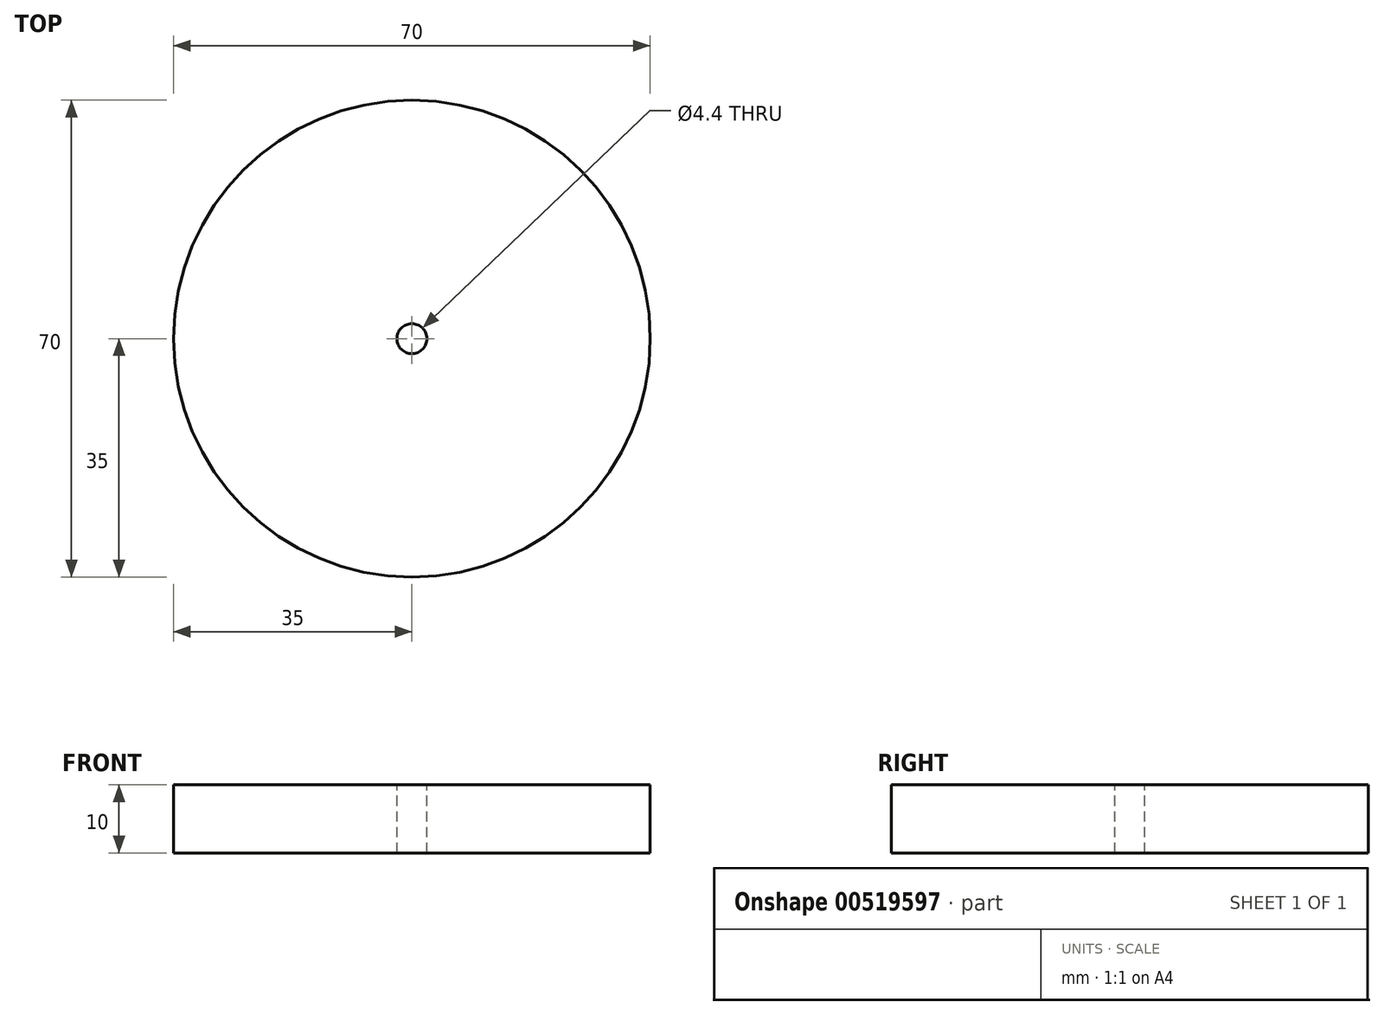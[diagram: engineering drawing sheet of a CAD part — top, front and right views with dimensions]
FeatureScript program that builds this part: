
annotation { "Feature Type Name" : "Feature", "Feature Type Description" : "" }
export const myFeature = defineFeature(function(context is Context, id is Id, definition is map)
    precondition{}
    {
        {
            var Q0;
            Q0=qCreatedBy(makeId("Top.planeOp"),FACE);
            var sketch = newSketch(context, id + "F0", { "sketchPlane" : qUnion([Q0])});
            skCircle(sketch, "E0", {"center": v(0, 0) * mm, "radius": 35 * mm});
            skSolve(sketch);
        }
        {
            var Q0;
            Q0=makeQuery(id+"F0.imprint","IMPRINT",FACE,{"disambiguationData":[TD([[makeQuery(id+"F0.imprint","IMPRINT",EDGE,{"derivedFrom":sQuery(id+"F0.wireOp",EDGE,"E0")}),1.0]])]});
            extrude(context, id + "F1", {"entities" : qUnion([Q0]), "depth" : 10 * mm, "offsetDistance" : 25.4 * mm});
        }
        {
            var Q0;
            Q0=makeQuery(id+"F1.opExtrude","CAP_FACE",FACE,{"disambiguationData":[OSD([sQuery(id+"F0.wireOp",EDGE,"E0")])],"isStart":false});
            var sketch = newSketch(context, id + "F2", { "sketchPlane" : qUnion([Q0])});
            skPoint(sketch, "E1", {"position": v(0, 0) * mm});
            skSolve(sketch);
        }
        {
            var Q0;
            Q0=sQuery(id+"F2.wireOp",VERTEX,"E1");
            var Q1;
            Q1=makeQuery(id+"F1.opExtrude","SWEPT_BODY",BODY,{"disambiguationData":[OSD([sQuery(id+"F0.wireOp",EDGE,"E0")])]});
            hole(context, id + "F3", {"style" : HoleStyle.SIMPLE, "endStyle" : HoleEndStyle.THROUGH, "standardTappedOrClearance" : lookupTablePath({ "fit" : "Normal", "standard" : "ISO", "engagement" : "75%", "pitch" : "0.8 mm", "size" : "M4", "type" : "Clearance" }), "standardBlindInLast" : lookupTablePath({ "fit" : "Standard", "standard" : "ISO", "engagement" : "75%", "pitch" : "0.8 mm", "size" : "M4", "type" : "Clearance" }), "holeDiameter" : 4.4 * mm, "showTappedDepth" : true, "isTappedThrough" : true, "tappedDepth" : 12.7 * mm, "tapClearance" : 3, "locations" : qUnion([Q0]), "scope" : qUnion([Q1])});
        }
    });
